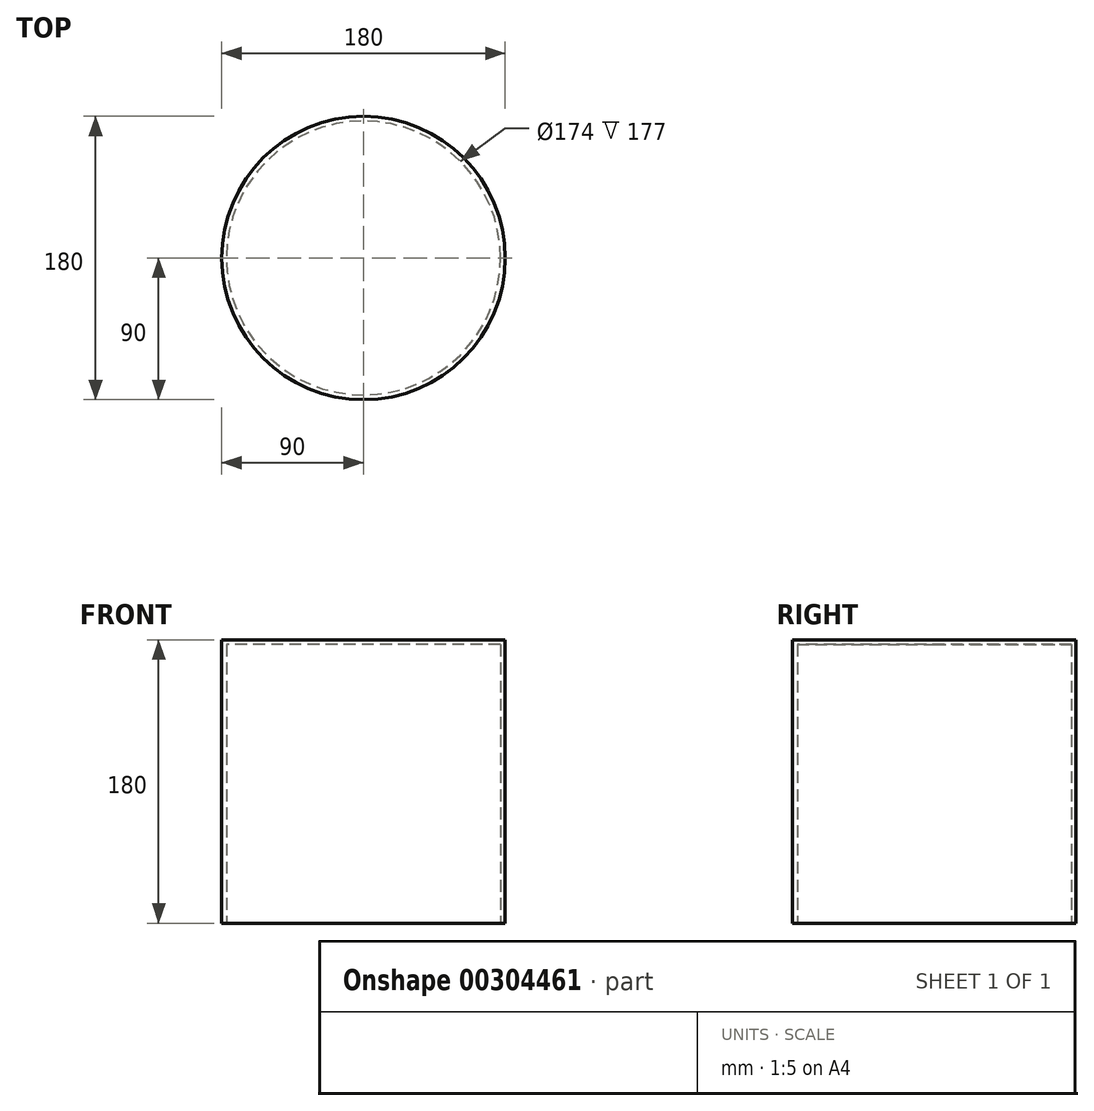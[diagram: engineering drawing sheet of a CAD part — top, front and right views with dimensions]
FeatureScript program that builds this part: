
annotation { "Feature Type Name" : "Feature", "Feature Type Description" : "" }
export const myFeature = defineFeature(function(context is Context, id is Id, definition is map)
    precondition{}
    {
        {
            var Q0;
            Q0=qCreatedBy(makeId("Top.planeOp"),FACE);
            var sketch = newSketch(context, id + "F0", { "sketchPlane" : qUnion([Q0])});
            skCircle(sketch, "E0", {"center": v(0, 0) * mm, "radius": 90 * mm});
            skSolve(sketch);
        }
        {
            var Q0;
            Q0 = qSketchRegion(id + "F0", true);
            extrude(context, id + "F1", {"entities" : qUnion([Q0]), "depth" : 180 * mm, "offsetDistance" : 25 * mm});
        }
        {
            var Q0;
            Q0=makeQuery(id+"F1.opExtrude","CAP_FACE",FACE,{"disambiguationData":[OSD([sQuery(id+"F0.wireOp",EDGE,"E0")])],"isStart":true});
            shell(context, id + "F2", {"entities" : qUnion([Q0]), "thickness" : 3 * mm});
        }
    });
